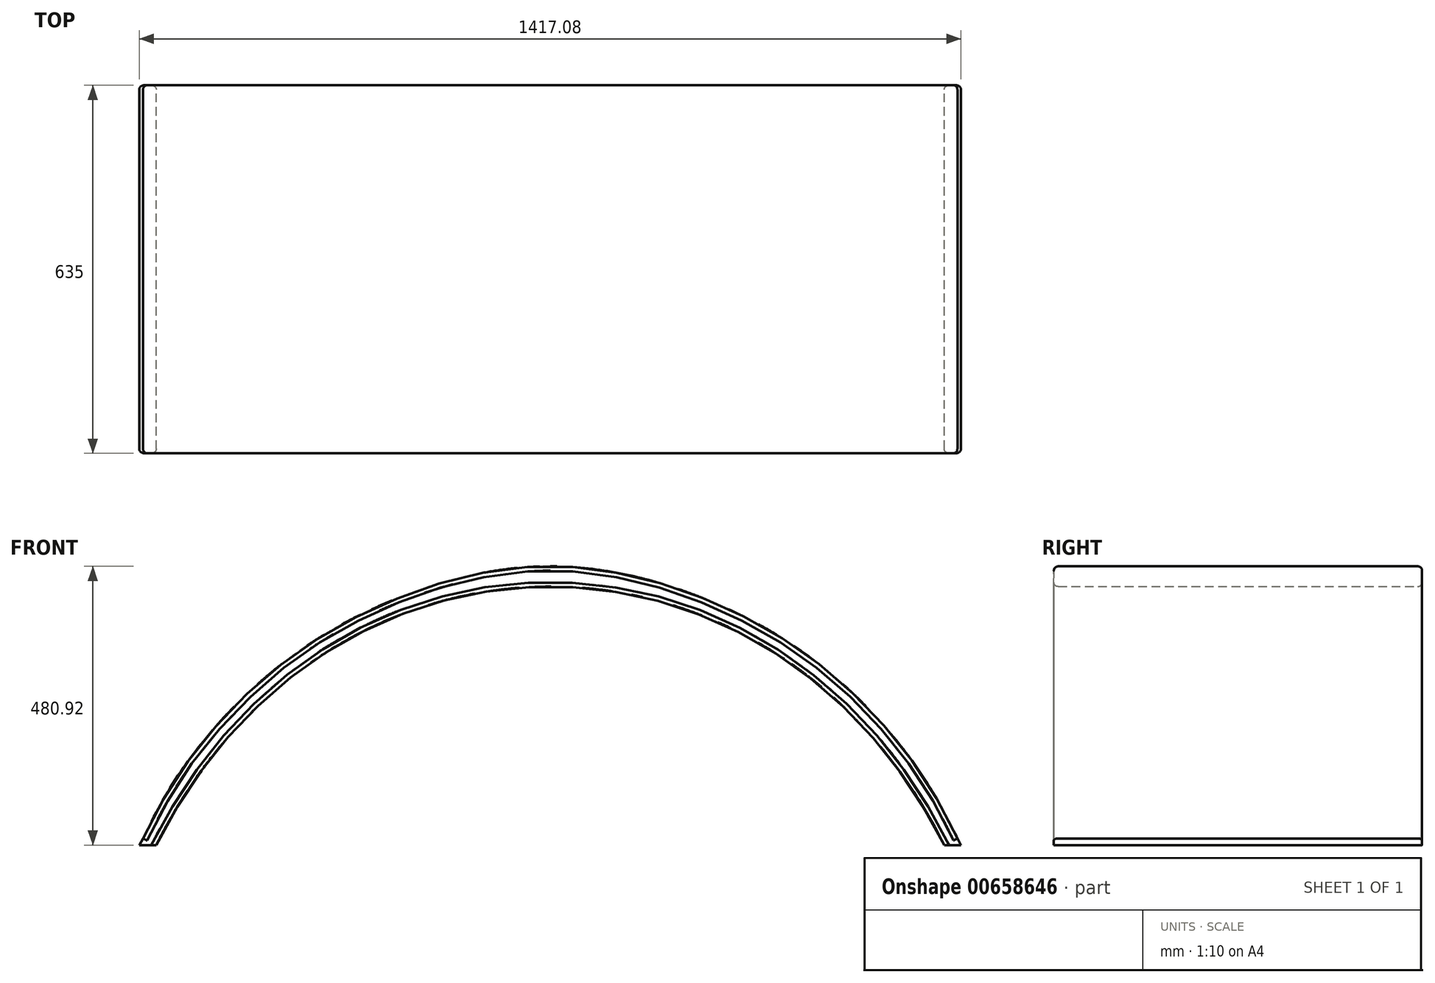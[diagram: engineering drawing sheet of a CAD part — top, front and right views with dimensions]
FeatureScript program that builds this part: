
annotation { "Feature Type Name" : "Feature", "Feature Type Description" : "" }
export const myFeature = defineFeature(function(context is Context, id is Id, definition is map)
    precondition{}
    {
        {
            var Q0;
            Q0=qCreatedBy(makeId("Front.planeOp"),FACE);
            var sketch = newSketch(context, id + "F0", { "sketchPlane" : qUnion([Q0])});
            skFitSpline(sketch, "E0", {"points": [v(-850.9, 879.88) * mm, v(508, 879.88) * mm], "startDerivative": vector(895.35, 1783.57) * mm, "endDerivative": vector(895.35, -1783.57) * mm});
            skFitSpline(sketch, "E1.0", {"points": [v(-873.6, 891.28) * mm, v(-854.46, 929.4) * mm, v(-812.41, 1001) * mm, v(-739.4, 1094.28) * mm, v(-657.83, 1173.38) * mm, v(-569.12, 1238.19) * mm, v(-474.69, 1288.65) * mm, v(-343.08, 1336.74) * mm, v(-171.45, 1360.8) * mm, v(0.18, 1336.74) * mm, v(131.79, 1288.65) * mm, v(226.22, 1238.19) * mm, v(314.93, 1173.38) * mm, v(396.5, 1094.28) * mm, v(469.51, 1001) * mm, v(511.56, 929.4) * mm, v(530.7, 891.28) * mm]});
            skLineSegment(sketch, "E2", {"start": v(508, 879.88) * mm, "end": v(536.89, 879.88) * mm});
            skLineSegment(sketch, "E3", {"start": v(530.7, 891.28) * mm, "end": v(536.89, 879.88) * mm});
            skLineSegment(sketch, "E4", {"start": v(-850.9, 879.88) * mm, "end": v(-880.2, 879.88) * mm});
            skLineSegment(sketch, "E5", {"start": v(-873.6, 891.28) * mm, "end": v(-880.2, 879.88) * mm});
            skSolve(sketch);
        }
        {
            var Q0;
            Q0=makeQuery(id+"F0.imprint","IMPRINT",FACE,{"disambiguationData":[TD([[makeQuery(id+"F0.imprint","IMPRINT",EDGE,{"derivedFrom":sQuery(id+"F0.wireOp",EDGE,"E0")}),1.0]])]});
            extrude(context, id + "F1", {"entities" : qUnion([Q0]), "depth" : 635 * mm, "offsetDistance" : 25.4 * mm});
        }
        {
            var Q0;
            Q0=makeQuery(id+"F1.opExtrude","CAP_EDGE",EDGE,{"disambiguationData":[OSD([sQuery(id+"F0.wireOp",EDGE,"E1.0")])],"isStart":false});
            var Q1;
            Q1=makeQuery(id+"F1.opExtrude","CAP_EDGE",EDGE,{"disambiguationData":[OSD([sQuery(id+"F0.wireOp",EDGE,"E0")])],"isStart":false});
            var Q2;
            Q2=makeQuery(id+"F1.opExtrude","CAP_EDGE",EDGE,{"disambiguationData":[OSD([sQuery(id+"F0.wireOp",EDGE,"E1.0")])],"isStart":true});
            var Q3;
            Q3=makeQuery(id+"F1.opExtrude","CAP_EDGE",EDGE,{"disambiguationData":[OSD([sQuery(id+"F0.wireOp",EDGE,"E0")])],"isStart":true});
            fillet(context, id + "F2", {"entities" : qUnion([Q0, Q1, Q2, Q3]), "radius" : 7.62 * mm, "tangentPropagation" : true, "allowEdgeOverflow" : false});
        }
    });
